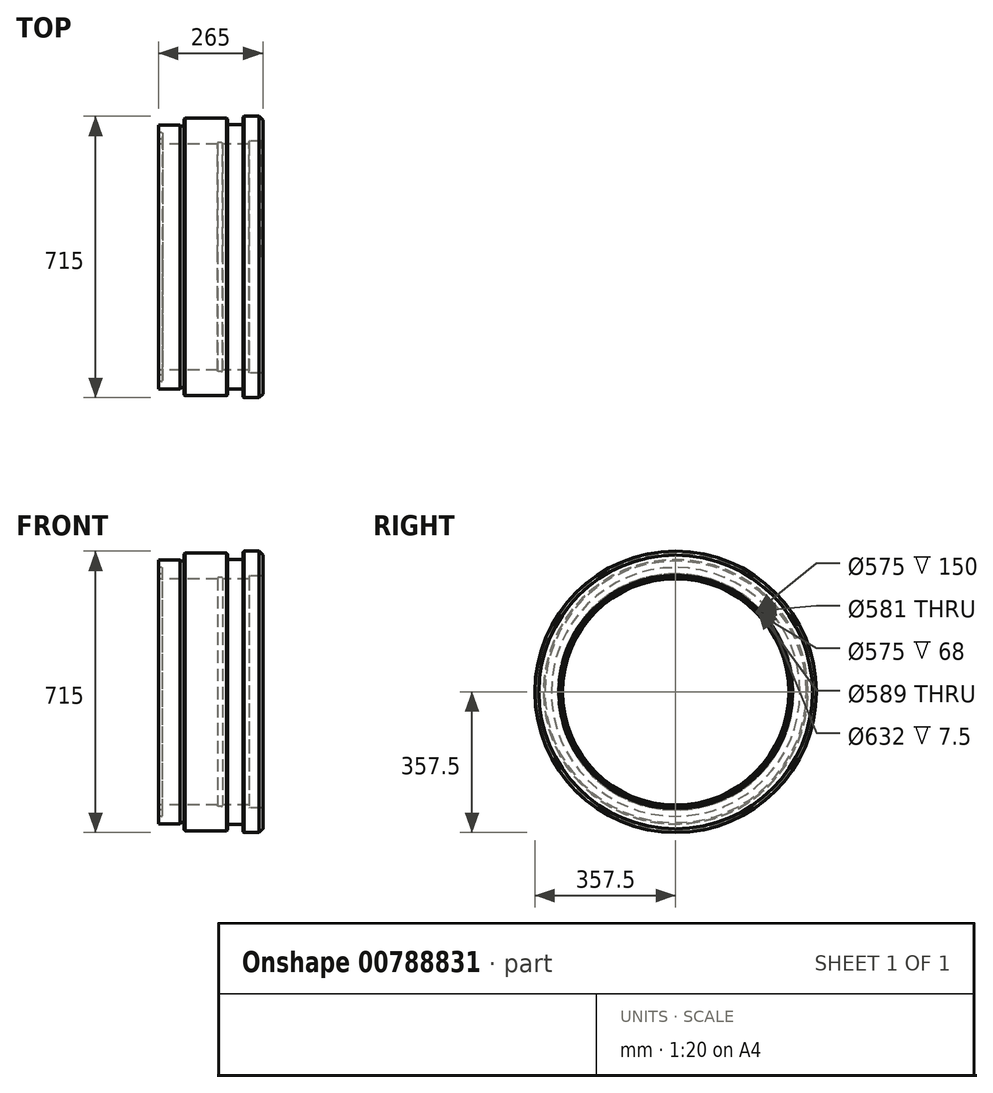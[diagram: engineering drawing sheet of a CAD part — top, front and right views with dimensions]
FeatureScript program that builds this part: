
annotation { "Feature Type Name" : "Feature", "Feature Type Description" : "" }
export const myFeature = defineFeature(function(context is Context, id is Id, definition is map)
    precondition{}
    {
        {
            var Q0;
            Q0=qCreatedBy(makeId("Front.planeOp"),FACE);
            var sketch = newSketch(context, id + "F0", { "sketchPlane" : qUnion([Q0])});
            skLineSegment(sketch, "E0", {"start": v(0, 287.5) * mm, "end": v(0, 335) * mm});
            skLineSegment(sketch, "E1", {"start": v(0, 335) * mm, "end": v(54.15, 335) * mm});
            skLineSegment(sketch, "E2", {"start": v(215, 338) * mm, "end": v(215, 357.5) * mm});
            skLineSegment(sketch, "E3", {"start": v(215, 357.5) * mm, "end": v(265, 357.5) * mm});
            skLineSegment(sketch, "E4", {"start": v(265, 357.5) * mm, "end": v(265, 294.5) * mm});
            skLineSegment(sketch, "E5", {"start": v(230, 287.5) * mm, "end": v(162, 287.5) * mm});
            skLineSegment(sketch, "E6", {"start": v(0, 0) * mm, "end": v(321.85, 0) * mm, "construction": true});
            skLineSegment(sketch, "E7", {"start": v(213, 336) * mm, "end": v(177, 336) * mm});
            skLineSegment(sketch, "E8", {"start": v(175, 338) * mm, "end": v(175, 352.5) * mm});
            skLineSegment(sketch, "E9", {"start": v(175, 352.5) * mm, "end": v(65, 352.5) * mm});
            skLineSegment(sketch, "E10", {"start": v(57.66, 332.15) * mm, "end": v(63.4, 332.15) * mm});
            skLineSegment(sketch, "E11", {"start": v(65, 352.5) * mm, "end": v(65, 333.75) * mm});
            skLineSegment(sketch, "E12", {"start": v(56.53, 332.62) * mm, "end": v(54.15, 335) * mm});
            skPoint(sketch, "E13.visualSharp", {"position": v(215, 336) * mm});
            skArc(sketch, "E13.filletArc", {"start": v(213, 336) * mm, "mid": v(214.41, 336.59) * mm, "end": v(215, 338) * mm});
            skPoint(sketch, "E14.visualSharp", {"position": v(175, 336) * mm});
            skArc(sketch, "E14.filletArc", {"start": v(175, 338) * mm, "mid": v(175.59, 336.59) * mm, "end": v(177, 336) * mm});
            skPoint(sketch, "E15.visualSharp", {"position": v(65, 332.15) * mm});
            skArc(sketch, "E15.filletArc", {"start": v(63.4, 332.15) * mm, "mid": v(64.53, 332.62) * mm, "end": v(65, 333.75) * mm});
            skPoint(sketch, "E16.visualSharp", {"position": v(57, 332.15) * mm});
            skArc(sketch, "E16.filletArc", {"start": v(56.53, 332.62) * mm, "mid": v(57.05, 332.27) * mm, "end": v(57.66, 332.15) * mm});
            skLineSegment(sketch, "E17", {"start": v(265, 294.5) * mm, "end": v(231.6, 294.5) * mm});
            skLineSegment(sketch, "E18", {"start": v(230, 292.9) * mm, "end": v(230, 287.5) * mm});
            skPoint(sketch, "E19.orphan", {"position": v(265, 287.5) * mm});
            skPoint(sketch, "E20.visualSharp", {"position": v(230, 294.5) * mm});
            skArc(sketch, "E20.filletArc", {"start": v(231.6, 294.5) * mm, "mid": v(230.47, 294.03) * mm, "end": v(230, 292.9) * mm});
            skLineSegment(sketch, "E21", {"start": v(150, 287.5) * mm, "end": v(150, 288.9) * mm});
            skLineSegment(sketch, "E22", {"start": v(151.6, 290.5) * mm, "end": v(160.4, 290.5) * mm});
            skLineSegment(sketch, "E23", {"start": v(162, 288.9) * mm, "end": v(162, 287.5) * mm});
            skLineSegment(sketch, "E24.trimOffspring", {"start": v(150, 287.5) * mm, "end": v(0, 287.5) * mm});
            skPoint(sketch, "E25.visualSharp", {"position": v(150, 290.5) * mm});
            skArc(sketch, "E25.filletArc", {"start": v(151.6, 290.5) * mm, "mid": v(150.47, 290.03) * mm, "end": v(150, 288.9) * mm});
            skPoint(sketch, "E26.visualSharp", {"position": v(162, 290.5) * mm});
            skArc(sketch, "E26.filletArc", {"start": v(162, 288.9) * mm, "mid": v(161.53, 290.03) * mm, "end": v(160.4, 290.5) * mm});
            skSolve(sketch);
        }
        {
            var Q0;
            Q0 = qSketchRegion(id + "F0", true);
            var Q1;
            Q1=sQuery(id+"F0.wireOp",EDGE,"E6");
            revolve(context, id + "F1", {"surfaceOperationType" : NewSurfaceOperationType.NEW, "entities" : qUnion([Q0]), "axis" : qUnion([Q1]), "revolveType" : RevolveType.FULL});
        }
        {
            var Q0;
            Q0=makeQuery(id+"F1.opRevolve","SWEPT_EDGE",EDGE,{"disambiguationData":[OSD([sQuery(id+"F0.wireOp",EDGE,"E8"),sQuery(id+"F0.wireOp",EDGE,"E9")])]});
            var Q1;
            Q1=makeQuery(id+"F1.opRevolve","SWEPT_EDGE",EDGE,{"disambiguationData":[OSD([sQuery(id+"F0.wireOp",EDGE,"E2"),sQuery(id+"F0.wireOp",EDGE,"E3")])]});
            var Q2;
            Q2=makeQuery(id+"F1.opRevolve","SWEPT_EDGE",EDGE,{"disambiguationData":[OSD([sQuery(id+"F0.wireOp",EDGE,"E9"),sQuery(id+"F0.wireOp",EDGE,"E11")])]});
            chamfer(context, id + "F2", {"entities" : qUnion([Q0, Q1, Q2]), "width" : 2 * mm, "tangentPropagation" : true});
        }
        {
            var Q0;
            Q0=makeQuery(id+"F1.opRevolve","SWEPT_EDGE",EDGE,{"disambiguationData":[OSD([sQuery(id+"F0.wireOp",EDGE,"E3"),sQuery(id+"F0.wireOp",EDGE,"E4")])]});
            chamfer(context, id + "F3", {"entities" : qUnion([Q0]), "width" : 10 * mm, "tangentPropagation" : true});
        }
        {
            var Q0;
            Q0=makeQuery(id+"F1.opRevolve","SWEPT_EDGE",EDGE,{"disambiguationData":[OSD([sQuery(id+"F0.wireOp",EDGE,"E4"),sQuery(id+"F0.wireOp",EDGE,"E17")])]});
            chamfer(context, id + "F4", {"entities" : qUnion([Q0]), "width" : 2 * mm, "tangentPropagation" : true});
        }
        {
            var Q0;
            Q0=qCreatedBy(makeId("Right.planeOp"),FACE);
            var sketch = newSketch(context, id + "F5", { "sketchPlane" : qUnion([Q0])});
            skCircle(sketch, "E27", {"center": v(0, 0) * mm, "radius": 316 * mm});
            skCircle(sketch, "E28", {"center": v(0, 0) * mm, "radius": 300 * mm});
            skSolve(sketch);
        }
        {
            var Q0;
            Q0 = qSketchRegion(id + "F5", true);
            extrude(context, id + "F6", {"entities" : qUnion([Q0]), "operationType" : NewBodyOperationType.REMOVE, "depth" : 9.5 * mm, "offsetDistance" : 25 * mm});
        }
        {
            var Q0;
            Q0=makeQuery(id+"F6.boolean.opBoolean","COPY",EDGE,{"derivedFrom":makeQuery(id+"F6.opExtrude","CAP_EDGE",EDGE,{"disambiguationData":[OSD([sQuery(id+"F5.wireOp",EDGE,"E28")])],"isStart":false})});
            var Q1;
            Q1=makeQuery(id+"F6.boolean.opBoolean","COPY",EDGE,{"derivedFrom":makeQuery(id+"F6.opExtrude","CAP_EDGE",EDGE,{"disambiguationData":[OSD([sQuery(id+"F5.wireOp",EDGE,"E27")])],"isStart":false})});
            fillet(context, id + "F7", {"entities" : qUnion([Q0, Q1]), "radius" : 2 * mm, "tangentPropagation" : true, "allowEdgeOverflow" : false});
        }
        {
            var Q0;
            Q0=makeQuery(id+"F6.boolean.opBoolean","COPY",EDGE,{"derivedFrom":makeQuery(id+"F6.opExtrude","CAP_EDGE",EDGE,{"disambiguationData":[OSD([sQuery(id+"F5.wireOp",EDGE,"E27")])],"isStart":true})});
            var Q1;
            Q1=makeQuery(id+"F6.boolean.opBoolean","COPY",EDGE,{"derivedFrom":makeQuery(id+"F6.opExtrude","CAP_EDGE",EDGE,{"disambiguationData":[OSD([sQuery(id+"F5.wireOp",EDGE,"E28")])],"isStart":true})});
            fillet(context, id + "F8", {"entities" : qUnion([Q0, Q1]), "radius" : 1 * mm, "tangentPropagation" : true, "allowEdgeOverflow" : false});
        }
    });
